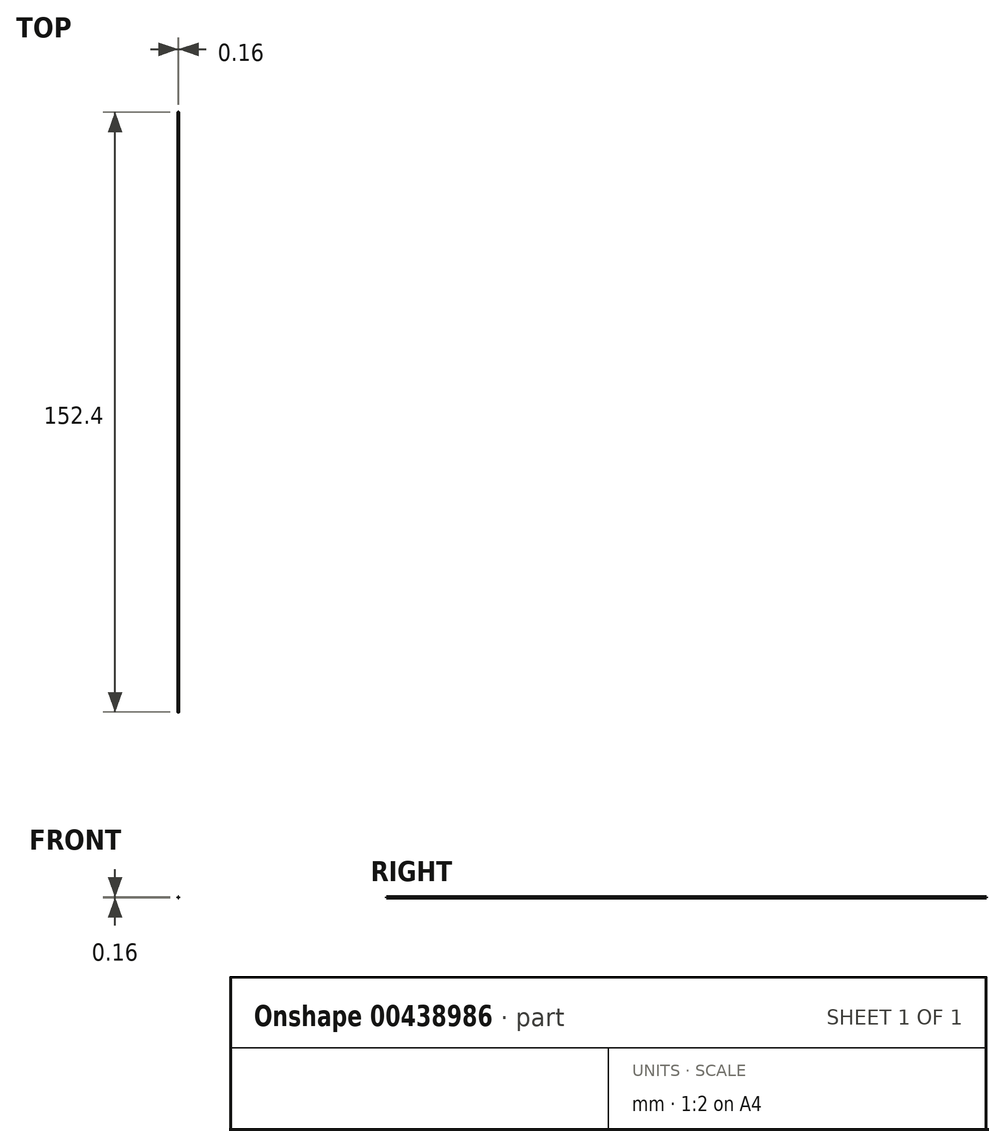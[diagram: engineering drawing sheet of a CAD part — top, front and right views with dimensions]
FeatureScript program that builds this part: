
annotation { "Feature Type Name" : "Feature", "Feature Type Description" : "" }
export const myFeature = defineFeature(function(context is Context, id is Id, definition is map)
    precondition{}
    {
        {
            var Q0;
            Q0=qCreatedBy(makeId("Front.planeOp"),FACE);
            var sketch = newSketch(context, id + "F0", { "sketchPlane" : qUnion([Q0])});
            skCircle(sketch, "E0", {"center": v(0, 0) * mm, "radius": 0.07 * mm});
            skSolve(sketch);
        }
        {
            var Q0;
            Q0 = qSketchRegion(id + "F0", true);
            extrude(context, id + "F1", {"entities" : qUnion([Q0]), "depth" : 152.4 * mm, "offsetDistance" : 25.4 * mm});
        }
        {
            var Q0;
            Q0=makeQuery(id+"F1.opExtrude","SWEPT_BODY",BODY,{"disambiguationData":[OSD([sQuery(id+"F0.wireOp",EDGE,"E0")])]});
            transform(context, id + "F2", {"entities" : qUnion([Q0]), "transformType" : TransformType.TRANSLATION_3D, "dx" : 0 * mm, "dy" : 76.2 * mm, "dz" : 0 * mm, "makeCopy" : false});
        }
    });
